# Revit family: PRD_FrankeWS_ShwrSts_FoldableShowerSeat_CNTX400A,B,C
name_source: partatom
category: Specialty Equipment
revit_build: Autodesk Revit 2018 (Build: 20190510_1515(x64)
units: mm (PartAtom-declared; Revit-internal decimal feet)

## family parameters
Cut with Voids When Loaded = No
Host = Face
OmniClass Number = 23.40.20.21
OmniClass Title = Toilet and Bath Specialties
Part Type = Normal
Room Calculation Point = No
Round Connector Dimension = Use Diameter
Shared = No

## types (3) — shared parameters
AssetType = Fixed
Category = Pr_40_20_06_83, Shower seats
Color = no colour
Default Elevation = 50 mm  [stored 0.164042 ft]
DurationUnit = year
EndingMaterial = PRD_AR_SyntheticBlack
Features = stainless steel, surface satin finished
Finish = satin finished
HiddenFixing = NO
IfcExportAs = IfcFurnitureType
IfcExportType = USERDEFINED
MainColor = stainless steel
Manufacturer = KWC Group AG
ManufacturerName = KWC Group AG
ManufacturerURL = www.kwc.com
Material = stainless steel
MaterialCode = 1.4301
MaterialThickness = 1.20 mm
NBSDescription = Shower seats
NBSReference = 45-35-72/352
NominalWidth = 484 mm  [stored 1.58793 ft]
PipeDiameter = 32  [stored 0.104987 ft]
PipeMaterial = PRD_AR_StainlessSteel_SatinFinished
ProductInformation = https://pim.kwc.com
SeatMaterial = PRD_AR_SyntheticWhite
URL = www.kwc.com
Uniclass2015Code = Pr_40_20_06_83
Uniclass2015Title = Shower seats
Uniclass2015Version = Products v1.10
Version = 1
WarrantyDurationUnit = year

## per-type parameters (varying)
| type | BIMObjectName | Back | CNTX400A | CNTX400B | CNTX400C | Description | Form | GrossWeight | Hinged | ModelNumber | Name | NetWeight | NominalDepth | NominalHeight | Size | TypeOfFixing | TypeOfGrabRail | TypeOfMounting |
| CNTX400A | PRD_AR_ShwrSts_FoldableShowerSeat_CNTX400A | NO | Yes | No | No | Foldable shower seat for wall mounting, stainless steel, surface satin finished, 32 mm pipe diameter, material thickness 1.2 mm, mounting through eight drilling holes, two prefixed white seat battens made of polyethylene, incl. stainless steel screws and dowels. | Wall mounted | 4.06 kg | YES | 2000057738 | Foldable Shower Seat CNTX400A | 3.41 kg | 526 mm  [stored 1.72572 ft] | 115 mm  [stored 0.377297 ft] | 526 x 115 x 484 mm | Screw | Seat | WALL-MOUNTING |
| CNTX400B | PRD_AR_ShwrSts_HangingShowerSeat_CNTX400B | YES | No | Yes | No | Hanging shower seat manufactured from grade EN 1.4301 (304) stainless steel, no grab rail included. Anti theft device. Seating and back: white battens made from polyethylene. | Hook mounted | 3.84 kg | NO | 2000057739 | Hanging Shower Seat CNTX400B | 3.84 kg | 520 mm  [stored 1.70604 ft] | 460 mm  [stored 1.50919 ft] | 520 x 460 x 484 mm | Catch | Seat | HOOK-MOUNTING |
| CNTX400C | PRD_AR_ShwrSts_HangingShowerSeat_CNTX400C | YES | No | No | Yes | Hanging back support manufactured from grade EN 1.4301 (304) stainless steel, no grab rail included. Anti theft device. Back: white battens made from polyethylene. | Hook mounted | 4.20 kg | NO | 2000057740 | Hanging Shower Seat CNTX400C | 3.80 kg | 158 mm | 427 mm  [stored 1.40092 ft] | 158 x 427 x 484 mm | Catch |  | HOOK-MOUNTING |

note: column(s) folded — value = type name in every type: Model, ModelReference

note: [stored X ft] marks values corroborated as IEEE doubles in the binary element streams (Revit-internal decimal feet)

## geometry (parser evidence)
native form markers: Sweep x2
no freeform markers — native parametric forms only
